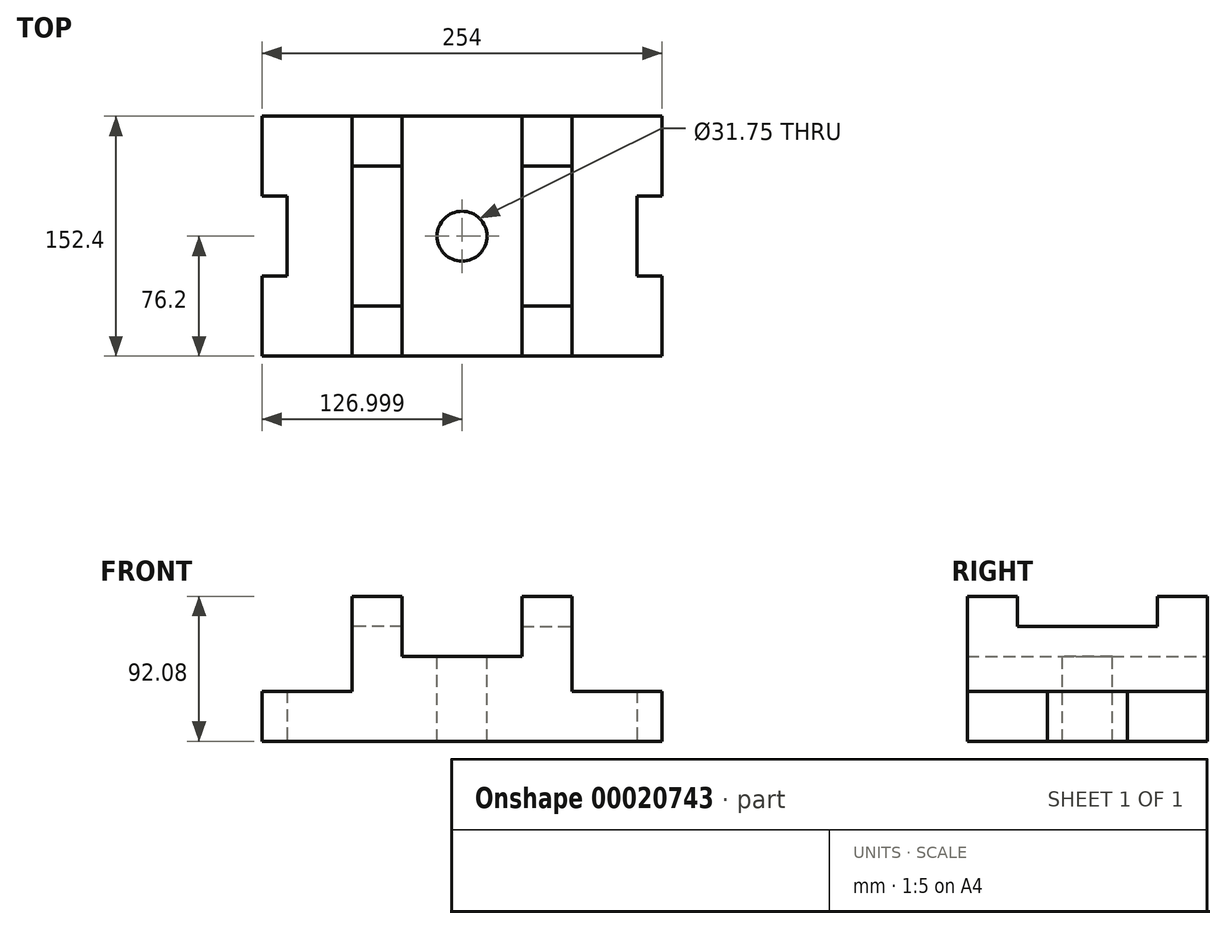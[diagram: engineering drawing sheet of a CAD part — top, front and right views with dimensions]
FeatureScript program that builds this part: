
annotation { "Feature Type Name" : "Feature", "Feature Type Description" : "" }
export const myFeature = defineFeature(function(context is Context, id is Id, definition is map)
    precondition{}
    {
        {
            var Q0;
            Q0=qCreatedBy(makeId("Top.planeOp"),FACE);
            var sketch = newSketch(context, id + "F0", { "sketchPlane" : qUnion([Q0])});
            skLineSegment(sketch, "E0.bottom", {"start": v(-60.37, 25.4) * mm, "end": v(50.75, 25.4) * mm});
            skLineSegment(sketch, "E0.top", {"start": v(-60.37, -50.8) * mm, "end": v(66.63, -50.8) * mm});
            skLineSegment(sketch, "E0.left", {"start": v(-60.37, 25.4) * mm, "end": v(-60.37, -50.8) * mm});
            skLineSegment(sketch, "E0.right", {"start": v(66.63, 0) * mm, "end": v(66.63, -50.8) * mm});
            skLineSegment(sketch, "E1", {"start": v(66.63, -50.8) * mm, "end": v(66.63, 0) * mm});
            skLineSegment(sketch, "E2", {"start": v(66.63, 0) * mm, "end": v(50.75, 0) * mm});
            skLineSegment(sketch, "E3", {"start": v(50.75, 0) * mm, "end": v(50.75, 25.4) * mm});
            skSolve(sketch);
        }
        {
            var Q0;
            Q0=makeQuery(id+"F0.imprint","IMPRINT",FACE,{"disambiguationData":[TD([[makeQuery(id+"F0.imprint","IMPRINT",EDGE,{"derivedFrom":sQuery(id+"F0.wireOp",EDGE,"E0.bottom")}),-1.0]])]});
            extrude(context, id + "F1", {"entities" : qUnion([Q0]), "depth" : 31.75 * mm});
        }
        {
            var Q0;
            Q0=makeQuery(id+"F1.opExtrude","CAP_FACE",FACE,{"disambiguationData":[OSD([sQuery(id+"F0.wireOp",EDGE,"E0.bottom"),sQuery(id+"F0.wireOp",EDGE,"E0.top"),sQuery(id+"F0.wireOp",EDGE,"E0.left"),sQuery(id+"F0.wireOp",EDGE,"E1"),sQuery(id+"F0.wireOp",EDGE,"E2"),sQuery(id+"F0.wireOp",EDGE,"E3")])],"isStart":false});
            var sketch = newSketch(context, id + "F2", { "sketchPlane" : qUnion([Q0])});
            skLineSegment(sketch, "E4", {"start": v(66.63, -50.8) * mm, "end": v(9.48, -50.8) * mm});
            skLineSegment(sketch, "E5", {"start": v(9.48, -50.8) * mm, "end": v(9.48, 25.4) * mm});
            skSolve(sketch);
        }
        {
            var Q0;
            {var subQ1=sQuery(id+"F2.wireOp",EDGE,"ef296ccc-6dff-42bd-a70b-d6d396a0b51e");Q0=makeQuery(id+"F2.imprint","IMPRINT",FACE,{"disambiguationData":[TD([[makeQuery(id+"F2.imprint","IMPRINT",EDGE,{"derivedFrom":subQ1}),-1.0]])]});}
            var Q1;
            {var subQ1=sQuery(id+"F2.wireOp",EDGE,"E5");Q1=makeQuery(id+"F2.imprint","IMPRINT",FACE,{"disambiguationData":[TD([[makeQuery(id+"F2.imprint","IMPRINT",EDGE,{"derivedFrom":subQ1}),1.0]])]});}
            extrude(context, id + "F3", {"entities" : qUnion([Q0, Q1]), "depth" : 60.32 * mm});
        }
        {
            var Q0;
            Q0=makeQuery(id+"F3.opExtrude","CAP_FACE",FACE,{"disambiguationData":[OSD([sQuery(id+"F0.wireOp",EDGE,"E0.bottom"),sQuery(id+"F0.wireOp",EDGE,"E0.top"),sQuery(id+"F0.wireOp",EDGE,"E0.left"),sQuery(id+"F2.wireOp",EDGE,"ef296ccc-6dff-42bd-a70b-d6d396a0b51e")])],"isStart":false});
            var sketch = newSketch(context, id + "F4", { "sketchPlane" : qUnion([Q0])});
            skLineSegment(sketch, "E6", {"start": v(9.48, -50.8) * mm, "end": v(9.48, -19.05) * mm});
            skLineSegment(sketch, "E7", {"start": v(9.48, -50.8) * mm, "end": v(-22.27, -50.8) * mm});
            skLineSegment(sketch, "E8", {"start": v(-22.27, -50.8) * mm, "end": v(-22.27, -19.05) * mm});
            skLineSegment(sketch, "E9", {"start": v(-22.27, -19.05) * mm, "end": v(9.48, -19.05) * mm});
            skLineSegment(sketch, "E10", {"start": v(-22.27, -19.05) * mm, "end": v(-22.27, 25.4) * mm});
            skSolve(sketch);
        }
        {
            var Q0;
            {var subQ4=sQuery(id+"F4.wireOp",EDGE,"E8");Q0=makeQuery(id+"F4.imprint","IMPRINT",FACE,{"disambiguationData":[TD([[makeQuery(id+"F4.imprint","IMPRINT",EDGE,{"derivedFrom":subQ4}),1.0]])]});}
            extrude(context, id + "F5", {"entities" : qUnion([Q0]), "operationType" : NewBodyOperationType.REMOVE, "oppositeDirection" : true, "depth" : 38.1 * mm});
        }
        {
            var Q0;
            {var subQ4=sQuery(id+"F4.wireOp",EDGE,"E9");Q0=makeQuery(id+"F4.imprint","IMPRINT",FACE,{"disambiguationData":[TD([[makeQuery(id+"F4.imprint","IMPRINT",EDGE,{"derivedFrom":subQ4}),1.0]])]});}
            extrude(context, id + "F6", {"entities" : qUnion([Q0]), "operationType" : NewBodyOperationType.REMOVE, "oppositeDirection" : true, "depth" : 19.05 * mm});
        }
        {
            var Q0;
            Q0=makeQuery(id+"F5.boolean.opBoolean","COPY",FACE,{"derivedFrom":makeQuery(id+"F5.opExtrude","CAP_FACE",FACE,{"disambiguationData":[OSD([sQuery(id+"F0.wireOp",EDGE,"E0.bottom"),sQuery(id+"F0.wireOp",EDGE,"E0.top"),sQuery(id+"F0.wireOp",EDGE,"E0.left"),sQuery(id+"F4.wireOp",EDGE,"E8"),sQuery(id+"F4.wireOp",EDGE,"E10")])],"isStart":false})});
            var sketch = newSketch(context, id + "F7", { "sketchPlane" : qUnion([Q0])});
            skArc(sketch, "E11", {"start": v(-60.37, 9.52) * mm, "mid": v(-49.15, 14.17) * mm, "end": v(-44.5, 25.4) * mm});
            skLineSegment(sketch, "E12", {"start": v(-60.37, 25.4) * mm, "end": v(-60.37, 9.52) * mm});
            skLineSegment(sketch, "E13", {"start": v(-60.37, 25.4) * mm, "end": v(-44.5, 25.4) * mm});
            skSolve(sketch);
        }
        {
            var Q0;
            Q0=makeQuery(id+"F7.imprint","IMPRINT",FACE,{"disambiguationData":[TD([[makeQuery(id+"F7.imprint","IMPRINT",EDGE,{"derivedFrom":sQuery(id+"F7.wireOp",EDGE,"E11")}),1.0]])]});
            extrude(context, id + "F8", {"entities" : qUnion([Q0]), "operationType" : NewBodyOperationType.REMOVE, "endBound" : BoundingType.THROUGH_ALL, "oppositeDirection" : true, "depth" : 25.4 * mm});
        }
        {
            var Q0;
            Q0=makeQuery(id+"F1.opExtrude","CAP_FACE",FACE,{"disambiguationData":[OSD([sQuery(id+"F0.wireOp",EDGE,"E0.bottom"),sQuery(id+"F0.wireOp",EDGE,"E0.top"),sQuery(id+"F0.wireOp",EDGE,"E0.left"),sQuery(id+"F0.wireOp",EDGE,"E1"),sQuery(id+"F0.wireOp",EDGE,"E2"),sQuery(id+"F0.wireOp",EDGE,"E3")])],"isStart":false});
            var sketch = newSketch(context, id + "F9", { "sketchPlane" : qUnion([Q0])});
            skArc(sketch, "E14", {"start": v(-60.37, 9.52) * mm, "mid": v(-49.15, 14.17) * mm, "end": v(-44.5, 25.4) * mm});
            skLineSegment(sketch, "E15", {"start": v(-60.37, 25.4) * mm, "end": v(-60.37, 9.52) * mm});
            skLineSegment(sketch, "E16", {"start": v(-60.37, 25.4) * mm, "end": v(-44.5, 25.4) * mm});
            skSolve(sketch);
        }
        {
            var Q0;
            Q0=makeQuery(id+"F9.imprint","IMPRINT",FACE,{"disambiguationData":[TD([[makeQuery(id+"F9.imprint","IMPRINT",EDGE,{"derivedFrom":sQuery(id+"F9.wireOp",EDGE,"E14")}),1.0]])]});
            extrude(context, id + "F10", {"entities" : qUnion([Q0]), "operationType" : NewBodyOperationType.REMOVE, "endBound" : BoundingType.THROUGH_ALL, "oppositeDirection" : true, "depth" : 25.4 * mm});
        }
        {
            var Q0;
            Q0=makeQuery(id+"F1.opExtrude","SWEPT_BODY",BODY,{"disambiguationData":[OSD([sQuery(id+"F0.wireOp",EDGE,"E0.bottom"),sQuery(id+"F0.wireOp",EDGE,"E0.top"),sQuery(id+"F0.wireOp",EDGE,"E0.left"),sQuery(id+"F0.wireOp",EDGE,"E1"),sQuery(id+"F0.wireOp",EDGE,"E2"),sQuery(id+"F0.wireOp",EDGE,"E3")])]});
            var Q1;
            Q1=makeQuery(id+"F3.opExtrude","SWEPT_BODY",BODY,{"disambiguationData":[OSD([sQuery(id+"F0.wireOp",EDGE,"E0.bottom"),sQuery(id+"F0.wireOp",EDGE,"E0.top"),sQuery(id+"F0.wireOp",EDGE,"E0.left"),sQuery(id+"F2.wireOp",EDGE,"E5")])]});
            var Q2;
            Q2=makeQuery(id+"F3.opExtrude","SWEPT_FACE",FACE,{"disambiguationData":[OSD([sQuery(id+"F0.wireOp",EDGE,"E0.bottom")])]});
            mirror(context, id + "F11", {"operationType" : NewBodyOperationType.ADD, "entities" : qUnion([Q0, Q1]), "mirrorPlane" : qUnion([Q2])});
        }
        {
            var Q0;
            Q0=makeQuery(id+"F1.opExtrude","SWEPT_BODY",BODY,{"disambiguationData":[OSD([sQuery(id+"F0.wireOp",EDGE,"E0.bottom"),sQuery(id+"F0.wireOp",EDGE,"E0.top"),sQuery(id+"F0.wireOp",EDGE,"E0.left"),sQuery(id+"F0.wireOp",EDGE,"E1"),sQuery(id+"F0.wireOp",EDGE,"E2"),sQuery(id+"F0.wireOp",EDGE,"E3")])]});
            var Q1;
            {var subQ0=sQuery(id+"F0.wireOp",EDGE,"E0.left");Q1=makeQuery(id+"F11.boolean.opBoolean","MERGE",FACE,{"derivedFrom":[makeQuery(id+"F3.opExtrude","SWEPT_FACE",FACE,{"disambiguationData":[OSD([subQ0])]}),makeQuery(id+"F1.opExtrude","SWEPT_FACE",FACE,{"disambiguationData":[OSD([subQ0])]})]});}
            mirror(context, id + "F12", {"operationType" : NewBodyOperationType.ADD, "entities" : qUnion([Q0]), "mirrorPlane" : qUnion([Q1])});
        }
    });
